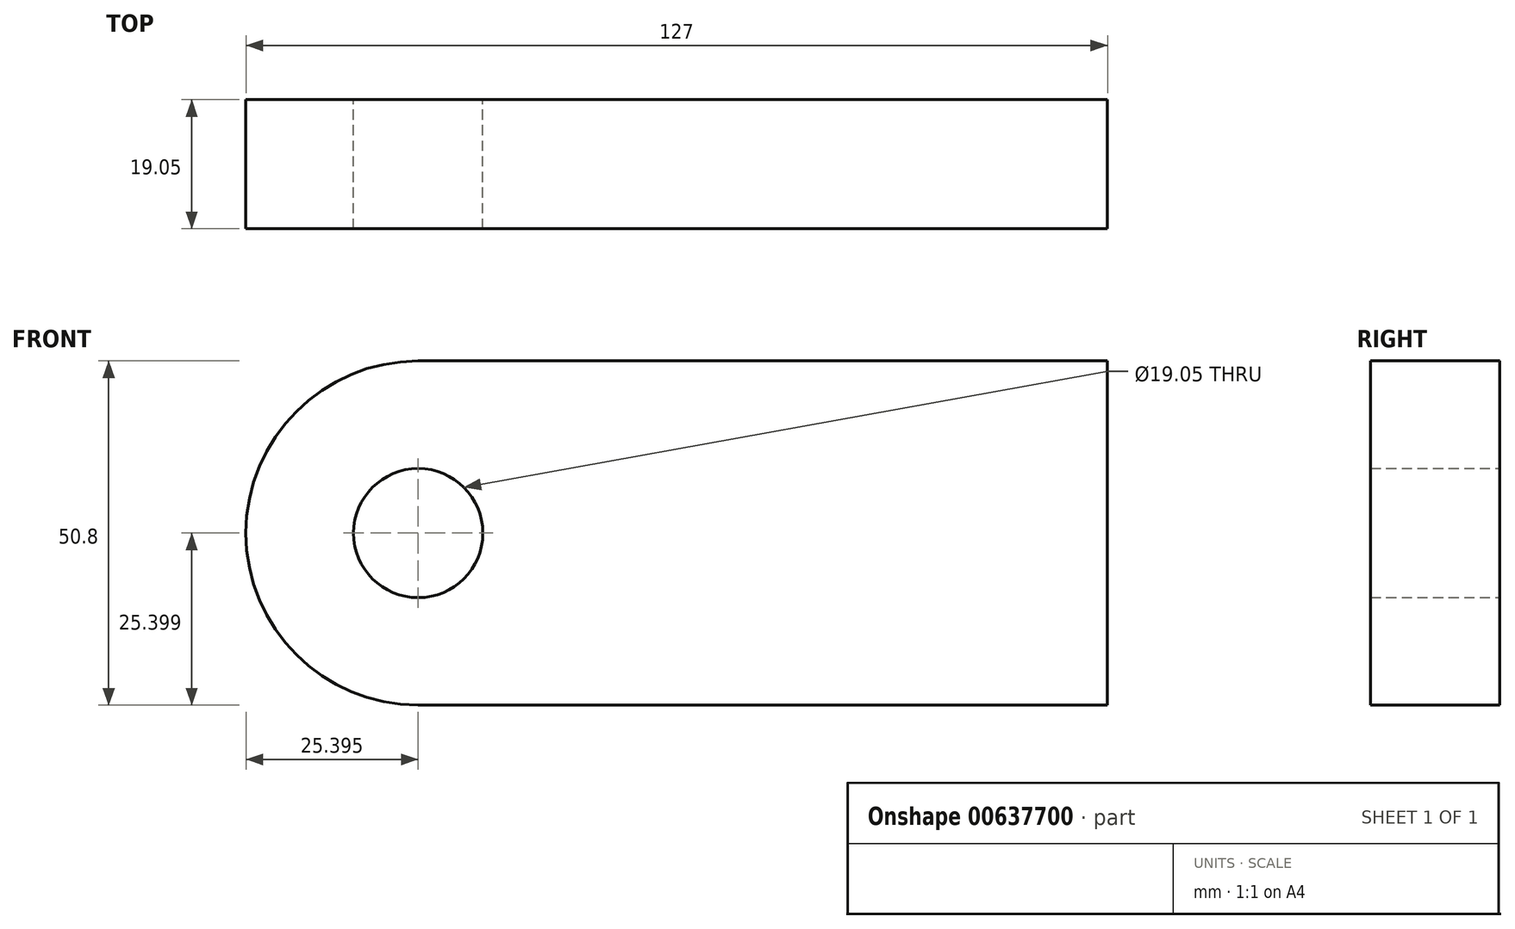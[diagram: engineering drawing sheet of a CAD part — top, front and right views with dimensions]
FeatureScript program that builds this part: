
annotation { "Feature Type Name" : "Feature", "Feature Type Description" : "" }
export const myFeature = defineFeature(function(context is Context, id is Id, definition is map)
    precondition{}
    {
        {
            var Q0;
            Q0=qCreatedBy(makeId("Front.planeOp"),FACE);
            var sketch = newSketch(context, id + "F0", { "sketchPlane" : qUnion([Q0])});
            skLineSegment(sketch, "E0", {"start": v(-21.75, 34.02) * mm, "end": v(79.85, 34.02) * mm});
            skLineSegment(sketch, "E1", {"start": v(79.85, 34.02) * mm, "end": v(79.85, -16.78) * mm});
            skLineSegment(sketch, "E2", {"start": v(79.85, -16.78) * mm, "end": v(-21.75, -16.78) * mm});
            skArc(sketch, "E3", {"start": v(-21.75, 34.02) * mm, "mid": v(-47.15, 8.62) * mm, "end": v(-21.75, -16.78) * mm});
            skCircle(sketch, "E4", {"center": v(-21.75, 8.62) * mm, "radius": 9.53 * mm});
            skSolve(sketch);
        }
        {
            var Q0;
            Q0=makeQuery(id+"F0.imprint","IMPRINT",FACE,{"disambiguationData":[TD([[makeQuery(id+"F0.imprint","IMPRINT",EDGE,{"derivedFrom":sQuery(id+"F0.wireOp",EDGE,"E0")}),-1.0]])]});
            extrude(context, id + "F1", {"entities" : qUnion([Q0]), "depth" : 19.05 * mm, "offsetDistance" : 25.4 * mm});
        }
    });
